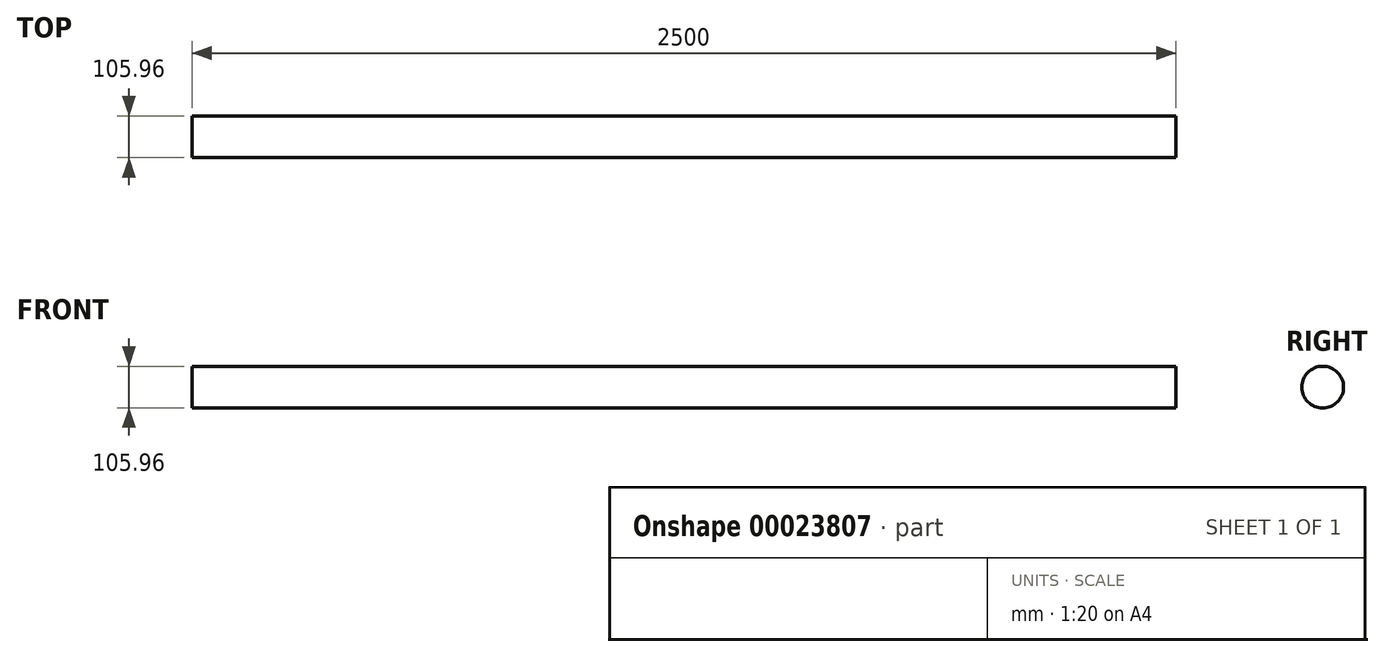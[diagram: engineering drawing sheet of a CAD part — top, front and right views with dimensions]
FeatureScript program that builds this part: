
annotation { "Feature Type Name" : "Feature", "Feature Type Description" : "" }
export const myFeature = defineFeature(function(context is Context, id is Id, definition is map)
    precondition{}
    {
        {
            var Q0;
            Q0=qCreatedBy(makeId("Right.planeOp"),FACE);
            var sketch = newSketch(context, id + "F0", { "sketchPlane" : qUnion([Q0])});
            skCircle(sketch, "E0", {"center": v(0, 0) * mm, "radius": 52.98 * mm});
            skSolve(sketch);
        }
        {
            var Q0;
            Q0 = qSketchRegion(id + "F0", true);
            extrude(context, id + "F1", {"entities" : qUnion([Q0]), "depth" : 2500 * mm});
        }
    });
